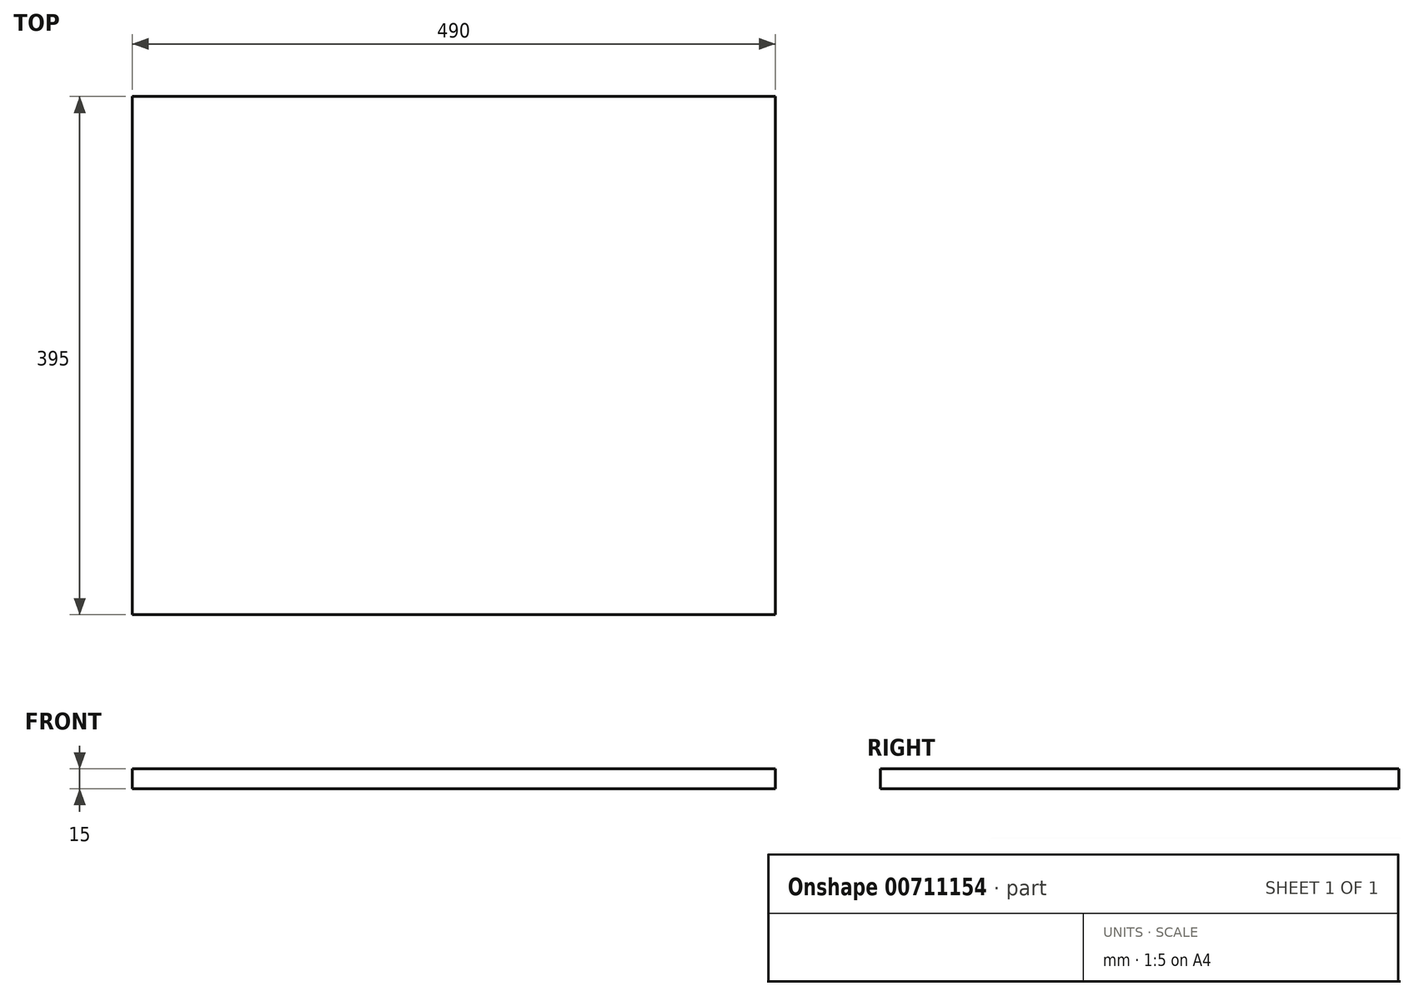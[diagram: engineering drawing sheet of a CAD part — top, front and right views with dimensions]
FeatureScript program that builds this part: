
annotation { "Feature Type Name" : "Feature", "Feature Type Description" : "" }
export const myFeature = defineFeature(function(context is Context, id is Id, definition is map)
    precondition{}
    {
        {
            var Q0;
            Q0=qCreatedBy(makeId("Top.planeOp"),FACE);
            var sketch = newSketch(context, id + "F0", { "sketchPlane" : qUnion([Q0])});
            skLineSegment(sketch, "E0.bottom", {"start": v(7.9, 0) * mm, "end": v(497.9, 0) * mm});
            skLineSegment(sketch, "E0.top", {"start": v(7.9, 395) * mm, "end": v(497.9, 395) * mm});
            skLineSegment(sketch, "E0.left", {"start": v(7.9, 0) * mm, "end": v(7.9, 395) * mm});
            skLineSegment(sketch, "E0.right", {"start": v(497.9, 0) * mm, "end": v(497.9, 395) * mm});
            skSolve(sketch);
        }
        {
            var Q0;
            Q0=makeQuery(id+"F0.imprint","IMPRINT",FACE,{"disambiguationData":[TD([[makeQuery(id+"F0.imprint","IMPRINT",EDGE,{"derivedFrom":sQuery(id+"F0.wireOp",EDGE,"E0.bottom")}),1.0]])]});
            extrude(context, id + "F1", {"entities" : qUnion([Q0]), "depth" : 15 * mm, "offsetDistance" : 25 * mm});
        }
    });
